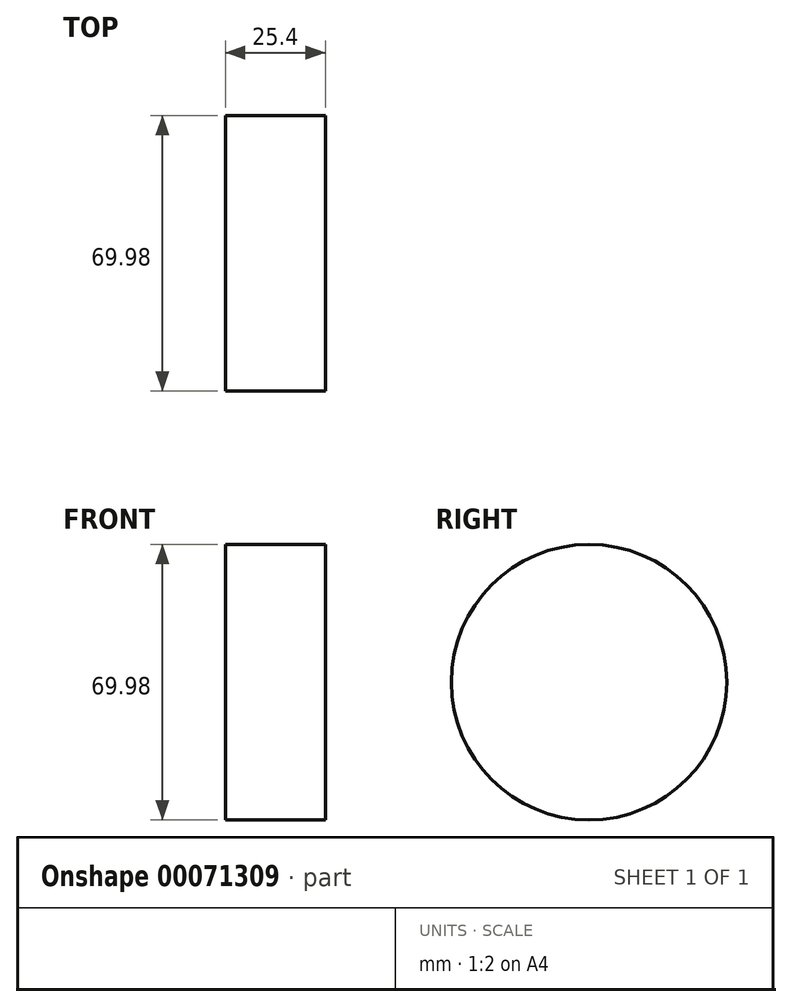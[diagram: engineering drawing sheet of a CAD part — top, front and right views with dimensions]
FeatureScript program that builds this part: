
annotation { "Feature Type Name" : "Feature", "Feature Type Description" : "" }
export const myFeature = defineFeature(function(context is Context, id is Id, definition is map)
    precondition{}
    {
        {
            var Q0;
            Q0=qCreatedBy(makeId("Right.planeOp"),FACE);
            var sketch = newSketch(context, id + "F0", { "sketchPlane" : qUnion([Q0])});
            skCircle(sketch, "E0", {"center": v(0, 0) * mm, "radius": 35 * mm});
            skSolve(sketch);
        }
        {
            var Q0;
            Q0 = qSketchRegion(id + "F0", true);
            extrude(context, id + "F1", {"entities" : qUnion([Q0]), "endBound" : BoundingType.SYMMETRIC, "depth" : 25.4 * mm});
        }
    });
